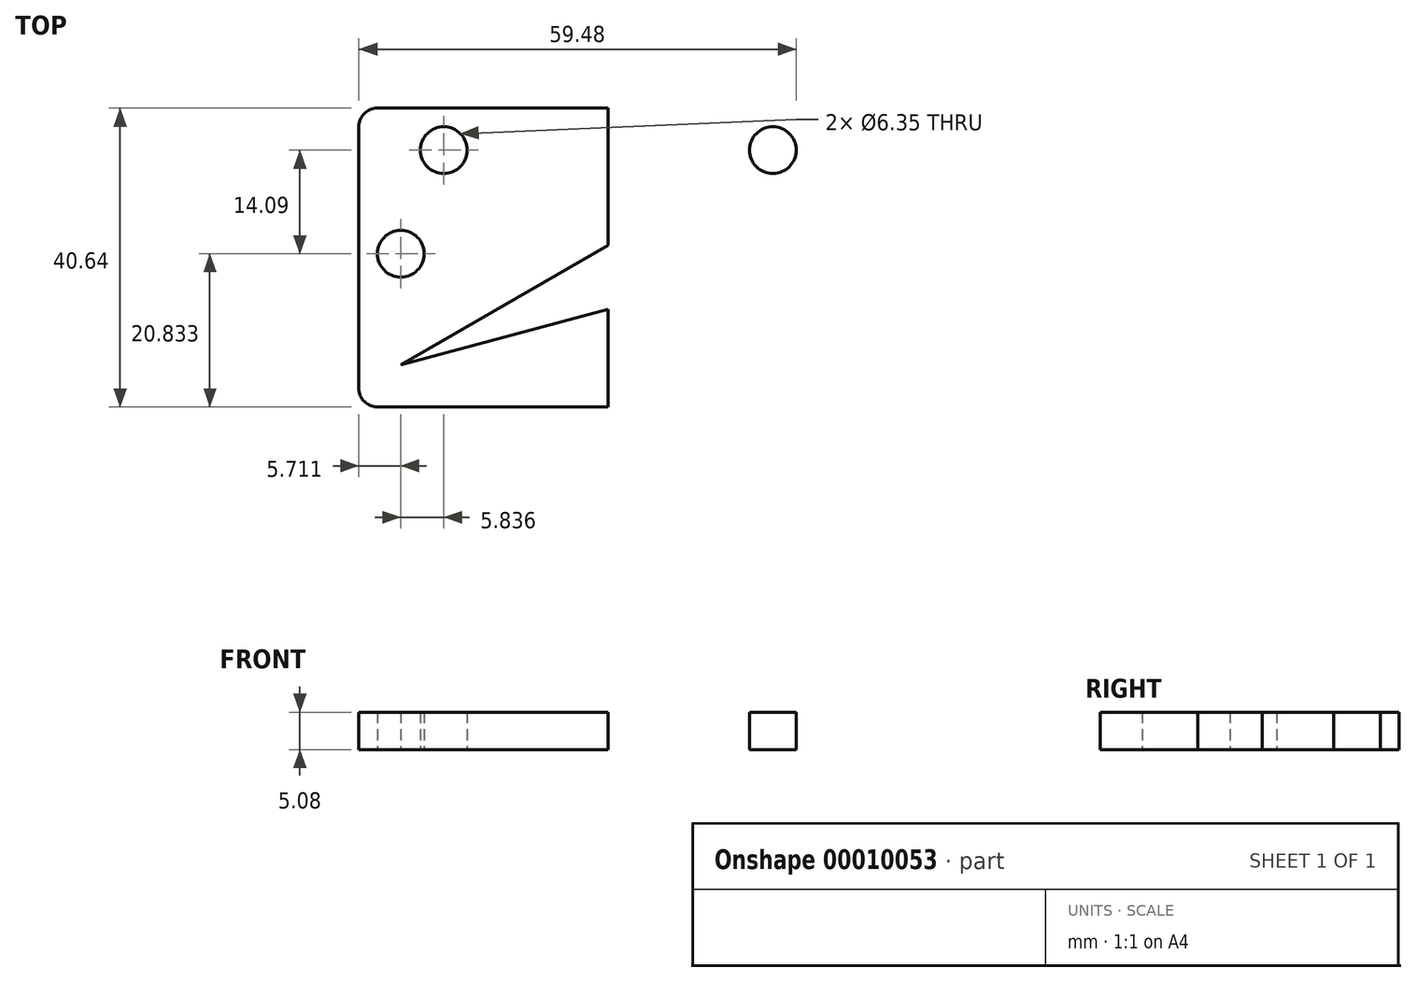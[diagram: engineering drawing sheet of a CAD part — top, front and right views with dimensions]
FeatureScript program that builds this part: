
annotation { "Feature Type Name" : "Feature", "Feature Type Description" : "" }
export const myFeature = defineFeature(function(context is Context, id is Id, definition is map)
    precondition{}
    {
        {
            var Q0;
            Q0=qCreatedBy(makeId("Top.planeOp"),FACE);
            var sketch = newSketch(context, id + "F0", { "sketchPlane" : qUnion([Q0])});
            skCircle(sketch, "E0.4.MirrorC", {"center": v(16.47, -27) * mm, "radius": 3.18 * mm});
            skCircle(sketch, "E0.8.MirrorC", {"center": v(67.06, 2.21) * mm, "radius": 3.18 * mm});
            skLineSegment(sketch, "E0.13.MirrorCS", {"start": v(67.06, 2.21) * mm, "end": v(16.47, -27) * mm});
            skLineSegment(sketch, "E0.14.MirrorCS", {"start": v(-44.94, -66.12) * mm, "end": v(121.92, 30.22) * mm, "construction": true});
            skLineSegment(sketch, "E0.15.MirrorCS", {"start": v(10.76, 5.39) * mm, "end": v(10.76, -30.17) * mm});
            skLineSegment(sketch, "E0.17.MirrorCS", {"start": v(76.08, -32.71) * mm, "end": v(13.3, -32.71) * mm});
            skLineSegment(sketch, "E0.18.MirrorCS", {"start": v(78.62, 5.39) * mm, "end": v(78.62, -30.17) * mm});
            skLineSegment(sketch, "E0.19.MirrorCS", {"start": v(76.08, 7.93) * mm, "end": v(13.3, 7.93) * mm});
            skLineSegment(sketch, "E1", {"start": v(-51.3, -41.87) * mm, "end": v(129.86, 6.67) * mm, "construction": true});
            skLineSegment(sketch, "E2", {"start": v(14.88, -24.25) * mm, "end": v(65.48, 4.96) * mm, "construction": true});
            skPoint(sketch, "E3.visualSharp", {"position": v(10.76, -32.71) * mm});
            skArc(sketch, "E3.filletArc", {"start": v(10.76, -30.17) * mm, "mid": v(11.5, -31.97) * mm, "end": v(13.3, -32.71) * mm});
            skPoint(sketch, "E4.visualSharp", {"position": v(78.62, -32.71) * mm});
            skArc(sketch, "E4.filletArc", {"start": v(76.08, -32.71) * mm, "mid": v(77.87, -31.97) * mm, "end": v(78.62, -30.17) * mm});
            skPoint(sketch, "E5.visualSharp", {"position": v(10.76, 7.93) * mm});
            skArc(sketch, "E5.filletArc", {"start": v(13.3, 7.93) * mm, "mid": v(11.5, 7.18) * mm, "end": v(10.76, 5.39) * mm});
            skPoint(sketch, "E6.visualSharp", {"position": v(78.62, 7.93) * mm});
            skArc(sketch, "E6.filletArc", {"start": v(78.62, 5.39) * mm, "mid": v(77.87, 7.18) * mm, "end": v(76.08, 7.93) * mm});
            skCircle(sketch, "E7", {"center": v(72.9, -11.88) * mm, "radius": 3.18 * mm});
            skLineSegment(sketch, "E8", {"start": v(16.47, -27) * mm, "end": v(72.9, -11.88) * mm});
            skPoint(sketch, "E9", {"position": v(44.69, 7.93) * mm});
            skLineSegment(sketch, "E10", {"start": v(44.69, 7.93) * mm, "end": v(44.69, -32.71) * mm});
            skCircle(sketch, "E11.0.MirrorC", {"center": v(72.9, -27) * mm, "radius": 3.18 * mm});
            skCircle(sketch, "E12.0.MirrorC", {"center": v(16.47, -11.88) * mm, "radius": 3.18 * mm});
            skCircle(sketch, "E13.0.MirrorC", {"center": v(22.3, 2.21) * mm, "radius": 3.18 * mm});
            skSolve(sketch);
        }
        {
            var Q0;
            Q0=makeQuery(id+"F0.imprint","IMPRINT",FACE,{"disambiguationData":[TD([[makeQuery(id+"F0.imprint","IMPRINT",EDGE,{"derivedFrom":sQuery(id+"F0.wireOp",EDGE,"E0.15.MirrorCS")}),1.0]])]});
            var Q1;
            {var subQ1=sQuery(id+"F0.wireOp",EDGE,"E0.4.MirrorC");var subQ5=sQuery(id+"F0.wireOp",EDGE,"E0.13.MirrorCS");var subQ7=makeQuery(id+"F0.imprint","INTERSECT",VERTEX,{"derivedFrom":[subQ1,subQ5]});Q1=makeQuery(id+"F0.imprint","IMPRINT",FACE,{"disambiguationData":[TD([[makeQuery(id+"F0.imprint","IMPRINT",EDGE,{"disambiguationData":[TD([[subQ7,-1.0]])],"derivedFrom":subQ1}),1.0]])]});}
            var Q2;
            Q2=makeQuery(id+"F0.imprint","IMPRINT",FACE,{"disambiguationData":[TD([[makeQuery(id+"F0.imprint","IMPRINT",EDGE,{"derivedFrom":sQuery(id+"F0.wireOp",EDGE,"E0.8.MirrorC")}),1.0]])]});
            extrude(context, id + "F1", {"entities" : qUnion([Q0, Q1, Q2]), "depth" : 5.08 * mm});
        }
    });
